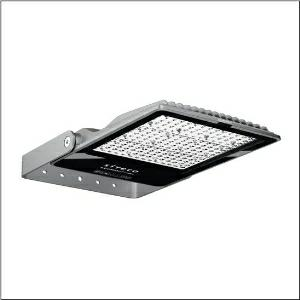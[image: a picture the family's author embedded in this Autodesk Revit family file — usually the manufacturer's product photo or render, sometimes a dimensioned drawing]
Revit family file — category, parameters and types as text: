
# Revit family: sicompact_31_midi___pl32_5xa7581e2k23_01f7
name_source: partatom
category: Lighting Fixtures
units: mm (PartAtom-declared; Revit-internal decimal feet)

## family parameters
Cut with Voids When Loaded = No
Host = Face
Light Source = No
Part Type = Normal
Room Calculation Point = No
Round Connector Dimension = Use Diameter
Shared = No

## types (1)
- SiCompact 31 midi  PL32 (1 x LED, 37000 lm, 243 W, 4000K)
    Apparent Load = 243 VA
    CIE Flux Codes = 32 69 98 100 100
    Color Rendering = 70
    Color Temperature = 4000K
    Default Elevation = 1800 mm
    Description = SiCompact 31 midi, floodlight, primary light control with lens, of plastic, of toughened safety glass, transparent, light distribution: PL32, light emission: direct distribution, primary light characteristic: asymmetric, installation type: surface-mounted, LED, High Power LED, rated luminous flux: 37.000lm, luminous efficacy: 152lm/W, light colour: 740, colour temperature: 4000K, control gear: ON/OFF, with cable, 3x 1.5mm², mains connection: 220..240V, AC, 50/60Hz, connection cable pre-assembled, cable length: 2m, rated input power: 243W, of diecast aluminium, specular, metallic grey (RAL 9006), length: 560mm, width: 330mm, height: 62mm, bracket, of sheet steel, coated, metallic grey (RAL 9006), ON/OFF, protection rating (complete): IP66, insulation class (complete): insulation class I (protective earthing), certification: CE, ENEC, impact resistance: IK08, permissible operating ambient temperature: -40..+45°C, packaging unit: 1 piece

Light Distribution: PL32
    Height = 62 mm  [stored 0.203412 ft]
    Lamp = 1 x LED
    Lamp Light Flux = 37000 lm
    Lamp Power = 243 W
    Lamp count = 1
    Length = 560 mm
    Luminous efficacy = 152 lm/W
    Manufacturer = Siteco
    ModVariant = No
    Model = 5XA7581E2K23
    Mounting Place = Wall
    Mounting Type = Surface mounted
    Number of Poles = 1
    OnlyDefault = Yes
    Power Factor = 1
    Product Name = SiCompact 31 midi | PL32
    Product group = floodlight | wall mounted
    ProductGroupID = 2002
    Protection Class = Protection class I
    Protection Degree = IP 66
    RLX_Detail_Level = 1
    RLX_Emergency_Light_Flux = 0 lm
    RLX_Emergency_Type = 0
    RLX_Emergency_Type_DB = No
    RlxData = <blob elided: 98221 chars, md5=d5866e47>
    Socket = socket
    Standby Power = 0 W
    System Light Flux = 37000 lm
    System Power = 243 W
    Type Comments = Product without accessories
    Type Image = l_1006415.jpg
    URL = http://relux.com
    VarID = ---
    Voltage = 0 V
    Weight = 0.00 kg
    Width = 333 mm

note: [stored X ft] marks values corroborated as IEEE doubles in the binary element streams (Revit-internal decimal feet)

## geometry (parser evidence)
native form markers: Blend x4, Sweep x10
no freeform markers — native parametric forms only
